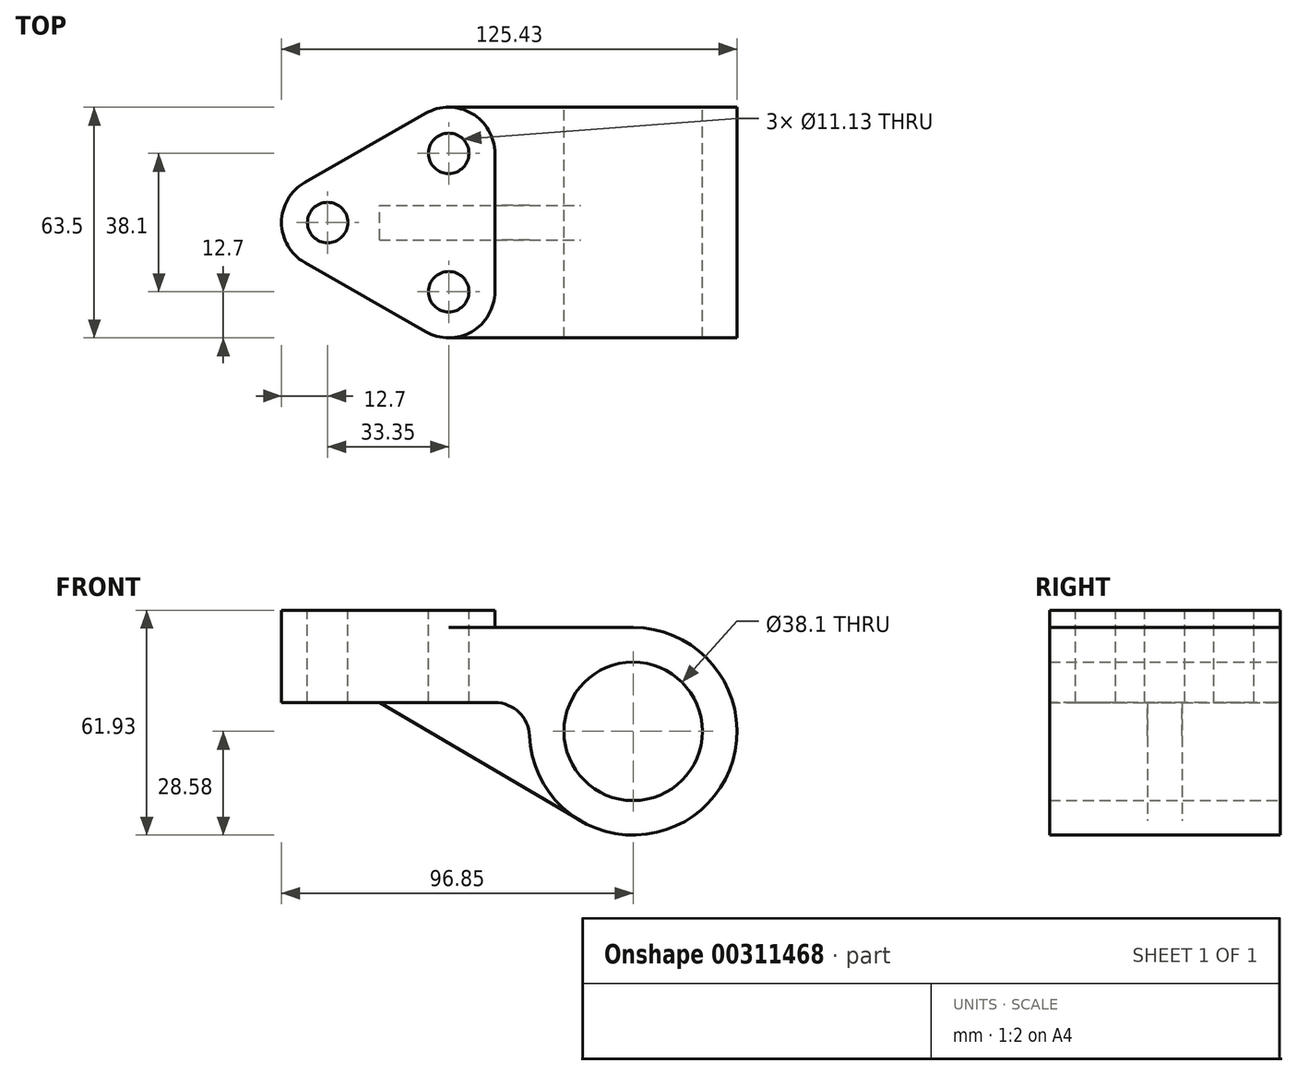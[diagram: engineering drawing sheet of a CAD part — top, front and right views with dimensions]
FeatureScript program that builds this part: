
annotation { "Feature Type Name" : "Feature", "Feature Type Description" : "" }
export const myFeature = defineFeature(function(context is Context, id is Id, definition is map)
    precondition{}
    {
        {
            var Q0;
            Q0=qCreatedBy(makeId("Front.planeOp"),FACE);
            var sketch = newSketch(context, id + "F0", { "sketchPlane" : qUnion([Q0])});
            skArc(sketch, "E0", {"start": v(-28.55, -1.2) * mm, "mid": v(20.63, -19.78) * mm, "end": v(0, 28.58) * mm});
            skLineSegment(sketch, "E1.bottom", {"start": v(-96.85, 28.58) * mm, "end": v(0, 28.58) * mm});
            skLineSegment(sketch, "E1.top", {"start": v(-96.85, 7.92) * mm, "end": v(-38.07, 7.92) * mm});
            skLineSegment(sketch, "E1.left", {"start": v(-96.85, 28.58) * mm, "end": v(-96.85, 7.92) * mm});
            skArc(sketch, "E2", {"start": v(-28.55, -1.2) * mm, "mid": v(-31.47, 5.27) * mm, "end": v(-38.07, 7.92) * mm});
            skCircle(sketch, "E3", {"center": v(0, 0) * mm, "radius": 19.05 * mm});
            skLineSegment(sketch, "E4", {"start": v(-69.85, 7.92) * mm, "end": v(-14.48, -24.63) * mm});
            skSolve(sketch);
        }
        {
            var Q0;
            {var subQ4=sQuery(id+"F0.wireOp",EDGE,"E1.bottom");Q0=makeQuery(id+"F0.imprint","IMPRINT",FACE,{"disambiguationData":[TD([[makeQuery(id+"F0.imprint","IMPRINT",EDGE,{"derivedFrom":subQ4}),-1.0]])]});}
            extrude(context, id + "F1", {"entities" : qUnion([Q0]), "endBound" : BoundingType.SYMMETRIC, "depth" : 63.5 * mm});
        }
        {
            var Q0;
            {var subQ0=sQuery(id+"F0.wireOp",EDGE,"E2");Q0=makeQuery(id+"F0.imprint","IMPRINT",FACE,{"disambiguationData":[TD([[makeQuery(id+"F0.imprint","IMPRINT",EDGE,{"derivedFrom":subQ0}),1.0]])]});}
            extrude(context, id + "F2", {"entities" : qUnion([Q0]), "operationType" : NewBodyOperationType.ADD, "endBound" : BoundingType.SYMMETRIC, "depth" : 9.52 * mm});
        }
        {
            var Q0;
            Q0=makeQuery(id+"F1.opExtrude","SWEPT_FACE",FACE,{"disambiguationData":[OSD([sQuery(id+"F0.wireOp",EDGE,"E1.bottom")])]});
            var sketch = newSketch(context, id + "F3", { "sketchPlane" : qUnion([Q0])});
            skLineSegment(sketch, "E5", {"start": v(-57.1, -30.08) * mm, "end": v(-90.45, -11.03) * mm});
            skLineSegment(sketch, "E6", {"start": v(-90.45, 11.03) * mm, "end": v(-57.1, 30.08) * mm});
            skLineSegment(sketch, "E7", {"start": v(-38.1, -19.05) * mm, "end": v(-38.1, 19.05) * mm});
            skArc(sketch, "E8", {"start": v(-57.1, -30.08) * mm, "mid": v(-44.42, -30.03) * mm, "end": v(-38.1, -19.05) * mm});
            skArc(sketch, "E9", {"start": v(-38.1, 19.05) * mm, "mid": v(-44.42, 30.03) * mm, "end": v(-57.1, 30.08) * mm});
            skArc(sketch, "E10", {"start": v(-90.45, 11.03) * mm, "mid": v(-96.85, 0) * mm, "end": v(-90.45, -11.03) * mm});
            skLineSegment(sketch, "E11", {"start": v(2.62, 0) * mm, "end": v(-160.92, 0) * mm, "construction": true});
            skPoint(sketch, "E11.endSnap0", {"position": v(-96.85, 0) * mm});
            skCircle(sketch, "E12", {"center": v(-50.8, -19.05) * mm, "radius": 5.56 * mm});
            skCircle(sketch, "E13", {"center": v(-84.15, 0) * mm, "radius": 5.56 * mm});
            skCircle(sketch, "E14", {"center": v(-50.8, 19.05) * mm, "radius": 5.56 * mm});
            skSolve(sketch);
        }
        {
            var Q0;
            {var subQ7=sQuery(id+"F3.wireOp",EDGE,"E5");Q0=makeQuery(id+"F3.imprint","IMPRINT",FACE,{"disambiguationData":[TD([[makeQuery(id+"F3.imprint","IMPRINT",EDGE,{"derivedFrom":subQ7}),1.0]])]});}
            var Q1;
            {var subQ6=sQuery(id+"F3.wireOp",EDGE,"E6");Q1=makeQuery(id+"F3.imprint","IMPRINT",FACE,{"disambiguationData":[TD([[makeQuery(id+"F3.imprint","IMPRINT",EDGE,{"derivedFrom":subQ6}),1.0]])]});}
            extrude(context, id + "F4", {"entities" : qUnion([Q0, Q1]), "operationType" : NewBodyOperationType.REMOVE, "endBound" : BoundingType.UP_TO_NEXT, "oppositeDirection" : true, "depth" : 25.4 * mm});
        }
        {
            var Q0;
            Q0=makeQuery(id+"F3.imprint","IMPRINT",FACE,{"disambiguationData":[TD([[makeQuery(id+"F3.imprint","IMPRINT",EDGE,{"derivedFrom":sQuery(id+"F3.wireOp",EDGE,"E13")}),1.0]])]});
            var Q1;
            Q1=makeQuery(id+"F3.imprint","IMPRINT",FACE,{"disambiguationData":[TD([[makeQuery(id+"F3.imprint","IMPRINT",EDGE,{"derivedFrom":sQuery(id+"F3.wireOp",EDGE,"E12")}),1.0]])]});
            var Q2;
            Q2=makeQuery(id+"F3.imprint","IMPRINT",FACE,{"disambiguationData":[TD([[makeQuery(id+"F3.imprint","IMPRINT",EDGE,{"derivedFrom":sQuery(id+"F3.wireOp",EDGE,"E14")}),1.0]])]});
            extrude(context, id + "F5", {"entities" : qUnion([Q0, Q1, Q2]), "operationType" : NewBodyOperationType.REMOVE, "endBound" : BoundingType.THROUGH_ALL, "oppositeDirection" : true, "depth" : 25.4 * mm});
        }
        {
            var Q0;
            {var subQ1=sQuery(id+"F3.wireOp",EDGE,"E5");Q0=makeQuery(id+"F3.imprint","IMPRINT",FACE,{"disambiguationData":[TD([[makeQuery(id+"F3.imprint","IMPRINT",EDGE,{"derivedFrom":subQ1}),-1.0]])]});}
            extrude(context, id + "F6", {"entities" : qUnion([Q0]), "operationType" : NewBodyOperationType.ADD, "depth" : 4.78 * mm});
        }
    });
